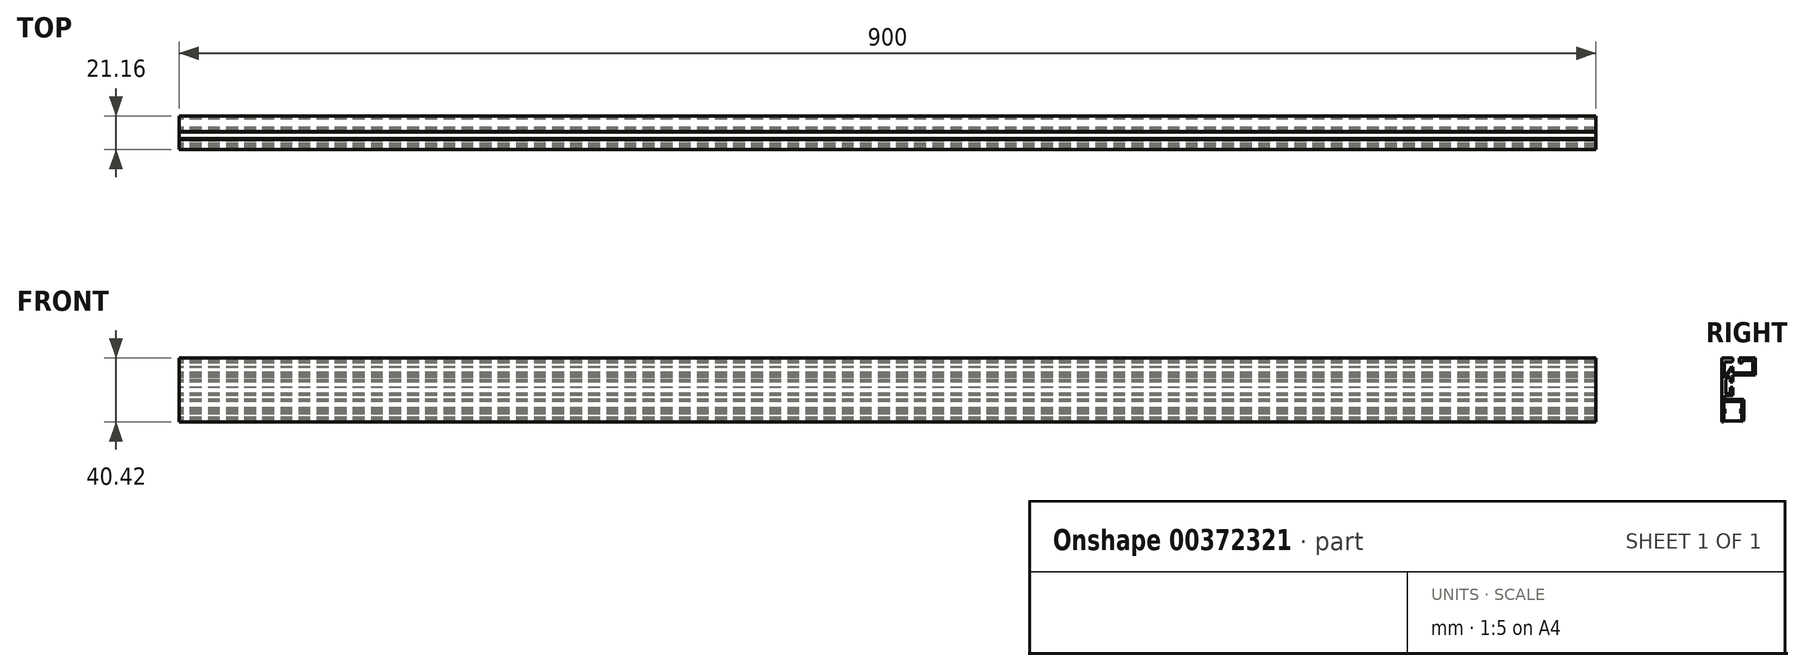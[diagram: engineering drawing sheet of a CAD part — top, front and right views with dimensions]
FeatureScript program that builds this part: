
annotation { "Feature Type Name" : "Feature", "Feature Type Description" : "" }
export const myFeature = defineFeature(function(context is Context, id is Id, definition is map)
    precondition{}
    {
        {
            var Q0;
            Q0=qCreatedBy(makeId("Right.planeOp"),FACE);
            var sketch = newSketch(context, id + "F0", { "sketchPlane" : qUnion([Q0])});
            skLineSegment(sketch, "E0.13", {"start": v(97.95, 20.2) * mm, "end": v(97.95, 9.58) * mm});
            skLineSegment(sketch, "E1.MirrorCS", {"start": v(83.74, 19.84) * mm, "end": v(83.78, 19.62) * mm});
            skLineSegment(sketch, "E2.MirrorCS", {"start": v(83.74, 18.76) * mm, "end": v(83.61, 18.51) * mm});
            skLineSegment(sketch, "E3.MirrorCS", {"start": v(83.78, 19.05) * mm, "end": v(83.74, 18.76) * mm});
            skLineSegment(sketch, "E4.MirrorCS", {"start": v(83.61, 18.51) * mm, "end": v(83.64, 18.5) * mm});
            skLineSegment(sketch, "E5.MirrorCS", {"start": v(83.2, 17.83) * mm, "end": v(83.2, 17.85) * mm});
            skLineSegment(sketch, "E6.MirrorCS", {"start": v(83.64, 18.5) * mm, "end": v(83.2, 17.83) * mm});
            skLineSegment(sketch, "E7.MirrorCS", {"start": v(83.8, 19.62) * mm, "end": v(83.8, 19.05) * mm});
            skLineSegment(sketch, "E8.MirrorCS", {"start": v(83.8, 19.05) * mm, "end": v(83.78, 19.05) * mm});
            skLineSegment(sketch, "E9.MirrorCS", {"start": v(77.92, -14.41) * mm, "end": v(77.8, -14.59) * mm});
            skLineSegment(sketch, "E10.MirrorCS", {"start": v(83.42, 20.16) * mm, "end": v(83.61, 20.04) * mm});
            skLineSegment(sketch, "E11.MirrorCS", {"start": v(82.78, 17.6) * mm, "end": v(82.78, 17.63) * mm});
            skLineSegment(sketch, "E12.MirrorCS", {"start": v(83.8, 19.62) * mm, "end": v(83.78, 19.62) * mm});
            skLineSegment(sketch, "E13.MirrorCS", {"start": v(78.16, -12.18) * mm, "end": v(78.3, -12.6) * mm});
            skLineSegment(sketch, "E14.MirrorCS", {"start": v(78.16, -14.02) * mm, "end": v(77.9, -14.41) * mm});
            skLineSegment(sketch, "E15.MirrorCS", {"start": v(83.2, 20.2) * mm, "end": v(83.42, 20.16) * mm});
            skLineSegment(sketch, "E16.MirrorCS", {"start": v(77.8, -11.61) * mm, "end": v(77.92, -11.79) * mm});
            skLineSegment(sketch, "E17.MirrorCS", {"start": v(83, 17.68) * mm, "end": v(82.78, 17.63) * mm});
            skLineSegment(sketch, "E18.MirrorCS", {"start": v(90.66, -18) * mm, "end": v(90.54, -18.5) * mm});
            skLineSegment(sketch, "E19.MirrorCS", {"start": v(78.3, -12.6) * mm, "end": v(78.36, -13.06) * mm});
            skLineSegment(sketch, "E20.MirrorCS", {"start": v(77.9, -11.79) * mm, "end": v(78.16, -12.18) * mm});
            skLineSegment(sketch, "E21.MirrorCS", {"start": v(83.2, 17.85) * mm, "end": v(83, 17.68) * mm});
            skLineSegment(sketch, "E22.MirrorCS", {"start": v(78.3, -13.6) * mm, "end": v(78.16, -14.02) * mm});
            skLineSegment(sketch, "E23.MirrorCS", {"start": v(83.61, 20.04) * mm, "end": v(83.74, 19.84) * mm});
            skLineSegment(sketch, "E24.MirrorCS", {"start": v(89.73, -14.59) * mm, "end": v(89.58, -14.41) * mm});
            skLineSegment(sketch, "E25.MirrorCS", {"start": v(90.56, -18.5) * mm, "end": v(90.54, -18.5) * mm});
            skLineSegment(sketch, "E26.MirrorCS", {"start": v(77.94, -11.74) * mm, "end": v(79.39, -13.5) * mm});
            skLineSegment(sketch, "E27.MirrorCS", {"start": v(78.36, -13.06) * mm, "end": v(78.36, -13.14) * mm});
            skLineSegment(sketch, "E28.MirrorCS", {"start": v(78.36, -13.14) * mm, "end": v(78.3, -13.6) * mm});
            skLineSegment(sketch, "E29.MirrorCS", {"start": v(77.9, -11.79) * mm, "end": v(77.92, -11.79) * mm});
            skLineSegment(sketch, "E30.MirrorCS", {"start": v(90.56, -18.5) * mm, "end": v(90.02, -20.01) * mm});
            skLineSegment(sketch, "E31.MirrorCS", {"start": v(89.58, -14.41) * mm, "end": v(89.6, -14.41) * mm});
            skLineSegment(sketch, "E32.MirrorCS", {"start": v(77.9, -14.41) * mm, "end": v(77.92, -14.41) * mm});
            skLineSegment(sketch, "E33.MirrorCS", {"start": v(89.33, -14.02) * mm, "end": v(89.19, -13.6) * mm});
            skLineSegment(sketch, "E34.MirrorCS", {"start": v(79.39, -13.5) * mm, "end": v(77.94, -15.25) * mm});
            skLineSegment(sketch, "E35.MirrorCS", {"start": v(89.58, -19.82) * mm, "end": v(89.58, -15.25) * mm});
            skLineSegment(sketch, "E36.MirrorCS", {"start": v(89.73, -20.01) * mm, "end": v(89.73, -14.59) * mm});
            skLineSegment(sketch, "E37.MirrorCS", {"start": v(89.14, -13.06) * mm, "end": v(89.14, -13.14) * mm});
            skLineSegment(sketch, "E38.MirrorCS", {"start": v(89.6, -14.41) * mm, "end": v(89.33, -14.02) * mm});
            skLineSegment(sketch, "E39.MirrorCS", {"start": v(90.02, -20.01) * mm, "end": v(89.73, -20.01) * mm});
            skLineSegment(sketch, "E40.MirrorCS", {"start": v(90.7, -6.88) * mm, "end": v(90.73, -6.88) * mm});
            skLineSegment(sketch, "E41.MirrorCS", {"start": v(89.19, -13.6) * mm, "end": v(89.14, -13.14) * mm});
            skLineSegment(sketch, "E42.MirrorCS", {"start": v(89.14, -13.06) * mm, "end": v(89.19, -12.6) * mm});
            skLineSegment(sketch, "E43.MirrorCS", {"start": v(90.68, -6.65) * mm, "end": v(90.7, -6.88) * mm});
            skLineSegment(sketch, "E44.MirrorCS", {"start": v(89.19, -12.6) * mm, "end": v(89.33, -12.18) * mm});
            skLineSegment(sketch, "E45.MirrorCS", {"start": v(89.6, -11.79) * mm, "end": v(89.58, -11.79) * mm});
            skLineSegment(sketch, "E46.MirrorCS", {"start": v(90.7, -17.5) * mm, "end": v(90.66, -18) * mm});
            skLineSegment(sketch, "E47.MirrorCS", {"start": v(89.33, -12.18) * mm, "end": v(89.6, -11.79) * mm});
            skLineSegment(sketch, "E48.MirrorCS", {"start": v(96.38, 11.05) * mm, "end": v(96.28, 10.95) * mm});
            skLineSegment(sketch, "E49.MirrorCS", {"start": v(90.41, -6.31) * mm, "end": v(90.59, -6.48) * mm});
            skLineSegment(sketch, "E50.MirrorCS", {"start": v(96.28, 10.95) * mm, "end": v(96.14, 10.9) * mm});
            skLineSegment(sketch, "E51.MirrorCS", {"start": v(89.58, -11.79) * mm, "end": v(89.73, -11.61) * mm});
            skLineSegment(sketch, "E52.MirrorCS", {"start": v(90.7, -17.5) * mm, "end": v(90.73, -17.5) * mm});
            skLineSegment(sketch, "E53.MirrorCS", {"start": v(96.43, 11.2) * mm, "end": v(96.46, 11.2) * mm});
            skLineSegment(sketch, "E54.MirrorCS", {"start": v(96.14, 10.9) * mm, "end": v(96.14, 10.88) * mm});
            skLineSegment(sketch, "E55.MirrorCS", {"start": v(96.43, 11.2) * mm, "end": v(96.38, 11.05) * mm});
            skLineSegment(sketch, "E56.MirrorCS", {"start": v(90.24, -6.21) * mm, "end": v(90.41, -6.31) * mm});
            skLineSegment(sketch, "E57.MirrorCS", {"start": v(89.58, -15.25) * mm, "end": v(88.1, -13.5) * mm});
            skLineSegment(sketch, "E58.MirrorCS", {"start": v(90.02, -6.19) * mm, "end": v(90.24, -6.21) * mm});
            skLineSegment(sketch, "E59.MirrorCS", {"start": v(90.73, -6.88) * mm, "end": v(90.73, -17.5) * mm});
            skLineSegment(sketch, "E60.MirrorCS", {"start": v(88.1, -13.5) * mm, "end": v(89.58, -11.74) * mm});
            skLineSegment(sketch, "E61.MirrorCS", {"start": v(90.02, -6.19) * mm, "end": v(90.02, -6.16) * mm});
            skLineSegment(sketch, "E62.MirrorCS", {"start": v(90.59, -6.48) * mm, "end": v(90.68, -6.65) * mm});
            skLineSegment(sketch, "E63.MirrorCS", {"start": v(89.58, -11.74) * mm, "end": v(89.58, -7.49) * mm});
            skLineSegment(sketch, "E64.MirrorCS", {"start": v(88.57, -18.8) * mm, "end": v(88.57, -15.62) * mm});
            skLineSegment(sketch, "E65.MirrorCS", {"start": v(80.7, -13.5) * mm, "end": v(78.95, -15.62) * mm});
            skLineSegment(sketch, "E66.MirrorCS", {"start": v(78.95, -11.37) * mm, "end": v(80.7, -13.5) * mm});
            skLineSegment(sketch, "E67.MirrorCS", {"start": v(87.52, -18.54) * mm, "end": v(88.57, -18.83) * mm});
            skLineSegment(sketch, "E68.MirrorCS", {"start": v(78.8, 7.96) * mm, "end": v(78.68, 7.93) * mm});
            skLineSegment(sketch, "E69.MirrorCS", {"start": v(78.53, 7.98) * mm, "end": v(78.43, 8.08) * mm});
            skLineSegment(sketch, "E70.MirrorCS", {"start": v(89.75, 17.5) * mm, "end": v(89.65, 17.36) * mm});
            skLineSegment(sketch, "E71.MirrorCS", {"start": v(89.73, -11.61) * mm, "end": v(89.73, -7.17) * mm});
            skLineSegment(sketch, "E72.MirrorCS", {"start": v(87.98, 17.36) * mm, "end": v(87.89, 17.5) * mm});
            skLineSegment(sketch, "E73.MirrorCS", {"start": v(87.81, 19.91) * mm, "end": v(87.86, 20.06) * mm});
            skLineSegment(sketch, "E74.MirrorCS", {"start": v(76.79, 20.2) * mm, "end": v(83.2, 20.2) * mm});
            skLineSegment(sketch, "E75.MirrorCS", {"start": v(87.86, 20.06) * mm, "end": v(87.96, 20.16) * mm});
            skLineSegment(sketch, "E76.MirrorCS", {"start": v(78.92, 8.05) * mm, "end": v(78.8, 7.96) * mm});
            skLineSegment(sketch, "E77.MirrorCS", {"start": v(87.81, 19.91) * mm, "end": v(87.81, 17.7) * mm});
            skLineSegment(sketch, "E78.MirrorCS", {"start": v(89.65, 17.36) * mm, "end": v(89.5, 17.26) * mm});
            skLineSegment(sketch, "E79.MirrorCS", {"start": v(83.32, 14.49) * mm, "end": v(83.61, 14.49) * mm});
            skLineSegment(sketch, "E80.MirrorCS", {"start": v(87.96, 20.16) * mm, "end": v(88.1, 20.2) * mm});
            skLineSegment(sketch, "E81.MirrorCS", {"start": v(87.89, 17.5) * mm, "end": v(87.84, 17.7) * mm});
            skLineSegment(sketch, "E82.MirrorCS", {"start": v(78.92, 8.05) * mm, "end": v(78.95, 8.05) * mm});
            skLineSegment(sketch, "E83.MirrorCS", {"start": v(88.13, 17.26) * mm, "end": v(87.98, 17.36) * mm});
            skLineSegment(sketch, "E84.MirrorCS", {"start": v(78.68, 7.93) * mm, "end": v(78.53, 7.98) * mm});
            skLineSegment(sketch, "E85.MirrorCS", {"start": v(88.33, 17.21) * mm, "end": v(89.3, 17.21) * mm});
            skLineSegment(sketch, "E86.MirrorCS", {"start": v(80.52, 8.08) * mm, "end": v(79.3, 6.24) * mm});
            skLineSegment(sketch, "E87.MirrorCS", {"start": v(77.8, -14.59) * mm, "end": v(77.8, -20.2) * mm});
            skLineSegment(sketch, "E88.MirrorCS", {"start": v(96.28, 18.66) * mm, "end": v(96.38, 18.56) * mm});
            skLineSegment(sketch, "E89.MirrorCS", {"start": v(82.78, 17.6) * mm, "end": v(78.38, 17.6) * mm});
            skLineSegment(sketch, "E90.MirrorCS", {"start": v(78.43, 8.08) * mm, "end": v(78.38, 8.23) * mm});
            skLineSegment(sketch, "E91.MirrorCS", {"start": v(88.57, -15.62) * mm, "end": v(86.8, -13.5) * mm});
            skLineSegment(sketch, "E92.MirrorCS", {"start": v(87.84, 17.7) * mm, "end": v(87.81, 17.7) * mm});
            skLineSegment(sketch, "E93.MirrorCS", {"start": v(86.8, -13.5) * mm, "end": v(88.57, -11.37) * mm});
            skLineSegment(sketch, "E94.MirrorCS", {"start": v(83.61, 14.49) * mm, "end": v(83.76, 14.44) * mm});
            skLineSegment(sketch, "E95.MirrorCS", {"start": v(88.33, 17.21) * mm, "end": v(88.13, 17.26) * mm});
            skLineSegment(sketch, "E96.MirrorCS", {"start": v(89.83, 17.7) * mm, "end": v(89.8, 17.7) * mm});
            skLineSegment(sketch, "E97.MirrorCS", {"start": v(89.5, 17.26) * mm, "end": v(89.3, 17.21) * mm});
            skLineSegment(sketch, "E98.MirrorCS", {"start": v(96.14, 18.71) * mm, "end": v(96.28, 18.66) * mm});
            skLineSegment(sketch, "E99.MirrorCS", {"start": v(78.95, -15.62) * mm, "end": v(78.95, -18.8) * mm});
            skLineSegment(sketch, "E100.MirrorCS", {"start": v(83.15, 14.39) * mm, "end": v(83.32, 14.49) * mm});
            skLineSegment(sketch, "E101.MirrorCS", {"start": v(77.94, -15.25) * mm, "end": v(77.94, -19.82) * mm});
            skLineSegment(sketch, "E102.MirrorCS", {"start": v(96.38, 18.56) * mm, "end": v(96.43, 18.42) * mm});
            skLineSegment(sketch, "E103.MirrorCS", {"start": v(77.8, -20.2) * mm, "end": v(76.79, -20.2) * mm});
            skLineSegment(sketch, "E104.MirrorCS", {"start": v(78.95, -18.83) * mm, "end": v(80, -18.54) * mm});
            skLineSegment(sketch, "E105.MirrorCS", {"start": v(88.57, -11.37) * mm, "end": v(88.57, -8.47) * mm});
            skLineSegment(sketch, "E106.MirrorCS", {"start": v(83.76, 14.44) * mm, "end": v(83.8, 14.3) * mm});
            skLineSegment(sketch, "E107.MirrorCS", {"start": v(89.83, 17.7) * mm, "end": v(89.83, 18.71) * mm});
            skLineSegment(sketch, "E108.MirrorCS", {"start": v(89.8, 17.7) * mm, "end": v(89.75, 17.5) * mm});
            skLineSegment(sketch, "E109.MirrorCS", {"start": v(77.94, -7.49) * mm, "end": v(77.94, -11.74) * mm});
            skLineSegment(sketch, "E110.MirrorCS", {"start": v(83.15, 14.39) * mm, "end": v(83.15, 14.41) * mm});
            skLineSegment(sketch, "E111.MirrorCS", {"start": v(96.43, 18.42) * mm, "end": v(96.46, 18.42) * mm});
            skLineSegment(sketch, "E112.MirrorCS", {"start": v(80, -18.54) * mm, "end": v(81.06, -18.34) * mm});
            skLineSegment(sketch, "E113.MirrorCS", {"start": v(77.8, -7.17) * mm, "end": v(77.8, -11.61) * mm});
            skLineSegment(sketch, "E114.MirrorCS", {"start": v(86.46, -18.34) * mm, "end": v(87.52, -18.54) * mm});
            skLineSegment(sketch, "E115.MirrorCS", {"start": v(80.52, 8.08) * mm, "end": v(81.4, 8.08) * mm});
            skLineSegment(sketch, "E116.MirrorCS", {"start": v(83.22, -18.12) * mm, "end": v(84.3, -18.12) * mm});
            skLineSegment(sketch, "E117.MirrorCS", {"start": v(84.3, -18.12) * mm, "end": v(85.38, -18.2) * mm});
            skLineSegment(sketch, "E118.MirrorCS", {"start": v(85.38, -18.2) * mm, "end": v(86.46, -18.34) * mm});
            skLineSegment(sketch, "E119.MirrorCS", {"start": v(78.95, -8.47) * mm, "end": v(78.95, -11.37) * mm});
            skLineSegment(sketch, "E120.MirrorCS", {"start": v(81.06, -18.34) * mm, "end": v(82.14, -18.2) * mm});
            skLineSegment(sketch, "E121.MirrorCS", {"start": v(82.14, -18.2) * mm, "end": v(83.22, -18.12) * mm});
            skLineSegment(sketch, "E122.MirrorCS", {"start": v(77.94, -19.82) * mm, "end": v(89.58, -19.82) * mm});
            skLineSegment(sketch, "E123.MirrorCS", {"start": v(82.29, 8.08) * mm, "end": v(81.4, 8.08) * mm});
            skLineSegment(sketch, "E124.MirrorCS", {"start": v(83.8, 14.3) * mm, "end": v(83.8, 10.88) * mm});
            skLineSegment(sketch, "E125.MirrorCS", {"start": v(82.29, 5.06) * mm, "end": v(82.29, 8.08) * mm});
            skLineSegment(sketch, "E126.MirrorCS", {"start": v(83.8, 5.06) * mm, "end": v(82.29, 5.06) * mm});
            skLineSegment(sketch, "E127.MirrorCS", {"start": v(89.83, 18.71) * mm, "end": v(96.14, 18.71) * mm});
            skLineSegment(sketch, "E128.MirrorCS", {"start": v(97.95, 20.2) * mm, "end": v(88.1, 20.2) * mm});
            skLineSegment(sketch, "E129.MirrorCS", {"start": v(83.8, 9.58) * mm, "end": v(83.8, 5.06) * mm});
            skLineSegment(sketch, "E130.MirrorCS", {"start": v(78.78, -3.66) * mm, "end": v(78.78, -6.16) * mm});
            skLineSegment(sketch, "E131.MirrorCS", {"start": v(82.29, -2.16) * mm, "end": v(82.29, 1.65) * mm});
            skLineSegment(sketch, "E132.MirrorCS", {"start": v(82.29, -2.16) * mm, "end": v(79.3, -2.16) * mm});
            skLineSegment(sketch, "E133.MirrorCS", {"start": v(83.8, -3.66) * mm, "end": v(78.78, -3.66) * mm});
            skLineSegment(sketch, "E134.MirrorCS", {"start": v(78.95, 8.05) * mm, "end": v(83.15, 14.41) * mm});
            skLineSegment(sketch, "E135.MirrorCS", {"start": v(82.29, 1.65) * mm, "end": v(83.8, 1.65) * mm});
            skLineSegment(sketch, "E136.MirrorCS", {"start": v(90.02, -6.16) * mm, "end": v(78.78, -6.16) * mm});
            skLineSegment(sketch, "E137.MirrorCS", {"start": v(83.8, 1.65) * mm, "end": v(83.8, -3.66) * mm});
            skLineSegment(sketch, "E138.MirrorCS", {"start": v(76.79, 20.2) * mm, "end": v(76.79, -20.2) * mm});
            skLineSegment(sketch, "E139.MirrorCS", {"start": v(77.8, -7.17) * mm, "end": v(89.73, -7.17) * mm});
            skPoint(sketch, "E140.MirrorP", {"position": v(89.11, -13.14) * mm});
            skLineSegment(sketch, "E141.MirrorCS", {"start": v(79.3, 6.24) * mm, "end": v(79.3, -2.16) * mm});
            skLineSegment(sketch, "E142.MirrorCS", {"start": v(83.8, 10.88) * mm, "end": v(96.14, 10.88) * mm});
            skLineSegment(sketch, "E143.MirrorCS", {"start": v(89.58, -7.49) * mm, "end": v(77.94, -7.49) * mm});
            skLineSegment(sketch, "E144.MirrorCS", {"start": v(88.57, -8.47) * mm, "end": v(78.95, -8.47) * mm});
            skPoint(sketch, "E145.MirrorP", {"position": v(82.29, 8.08) * mm});
            skLineSegment(sketch, "E146.MirrorCS", {"start": v(83.8, 9.58) * mm, "end": v(97.95, 9.58) * mm});
            skLineSegment(sketch, "E147.MirrorCS", {"start": v(78.38, 17.6) * mm, "end": v(78.38, 8.23) * mm});
            skPoint(sketch, "E148.MirrorP", {"position": v(89.11, -13.06) * mm});
            skPoint(sketch, "E149.MirrorP", {"position": v(83.05, 5.06) * mm});
            skLineSegment(sketch, "E150.MirrorCS", {"start": v(96.46, 18.42) * mm, "end": v(96.46, 11.2) * mm});
            skPoint(sketch, "E151.MirrorP", {"position": v(81.4, 8.08) * mm});
            skSolve(sketch);
        }
        {
            var Q0;
            Q0=qSketchRegion(id+"F0",true);
            extrude(context, id + "F1", {"entities" : qUnion([Q0]), "offsetDistance" : 25 * mm, "depth" : 900 * mm});
        }
    });
